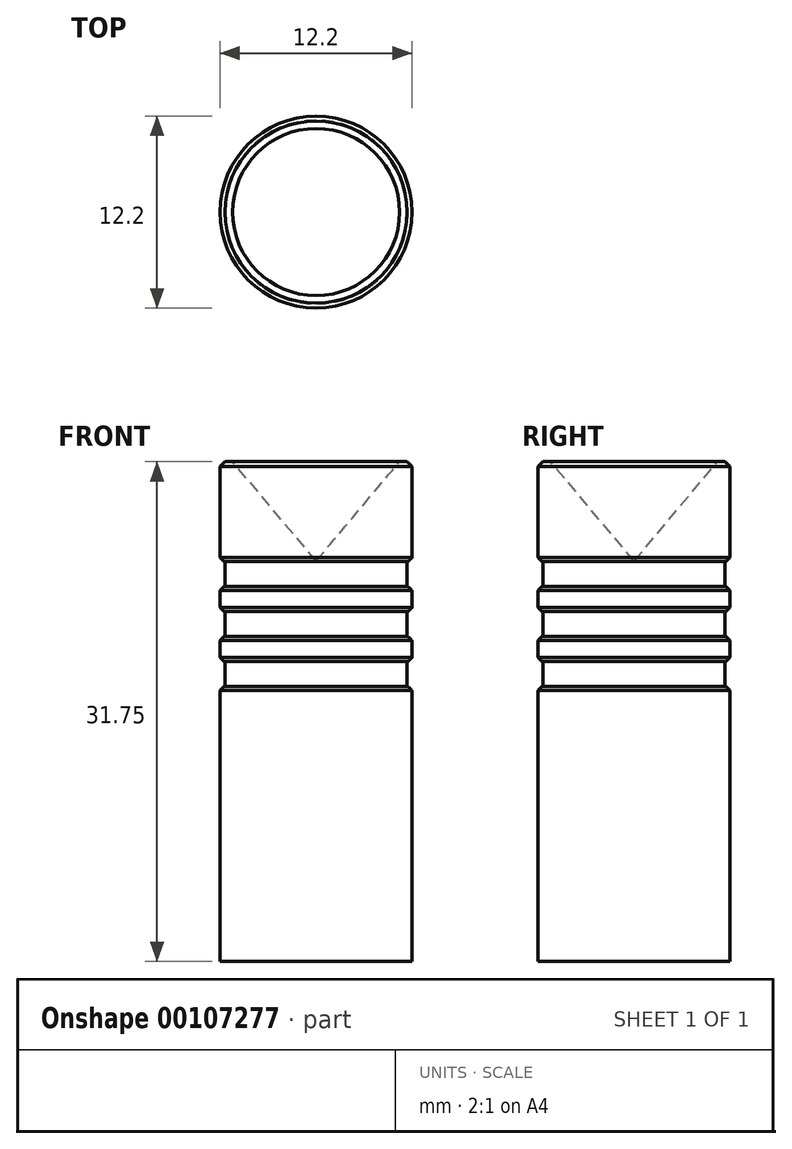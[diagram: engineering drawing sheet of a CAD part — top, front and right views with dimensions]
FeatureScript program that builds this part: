
annotation { "Feature Type Name" : "Feature", "Feature Type Description" : "" }
export const myFeature = defineFeature(function(context is Context, id is Id, definition is map)
    precondition{}
    {
        {
            var Q0;
            Q0=qCreatedBy(makeId("Front.planeOp"),FACE);
            var sketch = newSketch(context, id + "F0", { "sketchPlane" : qUnion([Q0])});
            skLineSegment(sketch, "E0", {"start": v(6.1, 31.75) * mm, "end": v(6.1, 0) * mm});
            skLineSegment(sketch, "E1", {"start": v(6.1, 0) * mm, "end": v(0, 0) * mm});
            skLineSegment(sketch, "E2", {"start": v(0, 0) * mm, "end": v(0, 25.43) * mm});
            skLineSegment(sketch, "E3", {"start": v(6.1, 31.75) * mm, "end": v(5.3, 31.75) * mm});
            skLineSegment(sketch, "E4", {"start": v(5.3, 31.75) * mm, "end": v(0, 25.43) * mm});
            skLineSegment(sketch, "E5.bottom", {"start": v(6.1, 25.4) * mm, "end": v(5.78, 25.4) * mm});
            skLineSegment(sketch, "E5.top", {"start": v(6.1, 23.81) * mm, "end": v(5.78, 23.81) * mm});
            skLineSegment(sketch, "E5.left", {"start": v(6.1, 25.4) * mm, "end": v(6.1, 23.81) * mm});
            skLineSegment(sketch, "E5.right", {"start": v(5.78, 25.4) * mm, "end": v(5.78, 23.81) * mm});
            skLineSegment(sketch, "E6.bottom", {"start": v(6.1, 22.23) * mm, "end": v(5.78, 22.23) * mm});
            skLineSegment(sketch, "E6.top", {"start": v(6.1, 20.64) * mm, "end": v(5.78, 20.64) * mm});
            skLineSegment(sketch, "E6.left", {"start": v(6.1, 22.23) * mm, "end": v(6.1, 20.64) * mm});
            skLineSegment(sketch, "E6.right", {"start": v(5.78, 22.23) * mm, "end": v(5.78, 20.64) * mm});
            skLineSegment(sketch, "E7.bottom", {"start": v(6.1, 19.05) * mm, "end": v(5.78, 19.05) * mm});
            skLineSegment(sketch, "E7.top", {"start": v(6.1, 17.46) * mm, "end": v(5.78, 17.46) * mm});
            skLineSegment(sketch, "E7.left", {"start": v(6.1, 19.05) * mm, "end": v(6.1, 17.46) * mm});
            skLineSegment(sketch, "E7.right", {"start": v(5.78, 19.05) * mm, "end": v(5.78, 17.46) * mm});
            skSolve(sketch);
        }
        {
            var Q0;
            {var subQ7=sQuery(id+"F0.wireOp",EDGE,"E1");Q0=makeQuery(id+"F0.imprint","IMPRINT",FACE,{"disambiguationData":[TD([[makeQuery(id+"F0.imprint","IMPRINT",EDGE,{"derivedFrom":subQ7}),-1.0]])]});}
            var Q1;
            Q1=sQuery(id+"F0.wireOp",EDGE,"E2");
            revolve(context, id + "F1", {"entities" : qUnion([Q0]), "axis" : qUnion([Q1]), "revolveType" : RevolveType.FULL});
        }
        {
            var Q0;
            Q0=makeQuery(id+"F1.opRevolve","SWEPT_EDGE",EDGE,{"disambiguationData":[OSD([sQuery(id+"F0.wireOp",EDGE,"E0"),sQuery(id+"F0.wireOp",EDGE,"E3")])]});
            chamfer(context, id + "F2", {"entities" : qUnion([Q0]), "width" : 0.32 * mm, "tangentPropagation" : true});
        }
        {
            var Q0;
            Q0=makeQuery(id+"F1.opRevolve","SWEPT_EDGE",EDGE,{"disambiguationData":[OSD([sQuery(id+"F0.wireOp",EDGE,"E0"),sQuery(id+"F0.wireOp",EDGE,"E5.bottom"),sQuery(id+"F0.wireOp",EDGE,"E5.left")])]});
            var Q1;
            Q1=makeQuery(id+"F1.opRevolve","SWEPT_EDGE",EDGE,{"disambiguationData":[OSD([sQuery(id+"F0.wireOp",EDGE,"E0"),sQuery(id+"F0.wireOp",EDGE,"E5.top"),sQuery(id+"F0.wireOp",EDGE,"E5.left")])]});
            var Q2;
            Q2=makeQuery(id+"F1.opRevolve","SWEPT_EDGE",EDGE,{"disambiguationData":[OSD([sQuery(id+"F0.wireOp",EDGE,"E0"),sQuery(id+"F0.wireOp",EDGE,"E6.bottom"),sQuery(id+"F0.wireOp",EDGE,"E6.left")])]});
            var Q3;
            Q3=makeQuery(id+"F1.opRevolve","SWEPT_EDGE",EDGE,{"disambiguationData":[OSD([sQuery(id+"F0.wireOp",EDGE,"E0"),sQuery(id+"F0.wireOp",EDGE,"E6.top"),sQuery(id+"F0.wireOp",EDGE,"E6.left")])]});
            var Q4;
            Q4=makeQuery(id+"F1.opRevolve","SWEPT_EDGE",EDGE,{"disambiguationData":[OSD([sQuery(id+"F0.wireOp",EDGE,"E0"),sQuery(id+"F0.wireOp",EDGE,"E7.bottom"),sQuery(id+"F0.wireOp",EDGE,"E7.left")])]});
            var Q5;
            Q5=makeQuery(id+"F1.opRevolve","SWEPT_EDGE",EDGE,{"disambiguationData":[OSD([sQuery(id+"F0.wireOp",EDGE,"E0"),sQuery(id+"F0.wireOp",EDGE,"E7.top"),sQuery(id+"F0.wireOp",EDGE,"E7.left")])]});
            chamfer(context, id + "F3", {"entities" : qUnion([Q0, Q1, Q2, Q3, Q4, Q5]), "width" : 0.25 * mm, "tangentPropagation" : true});
        }
    });
